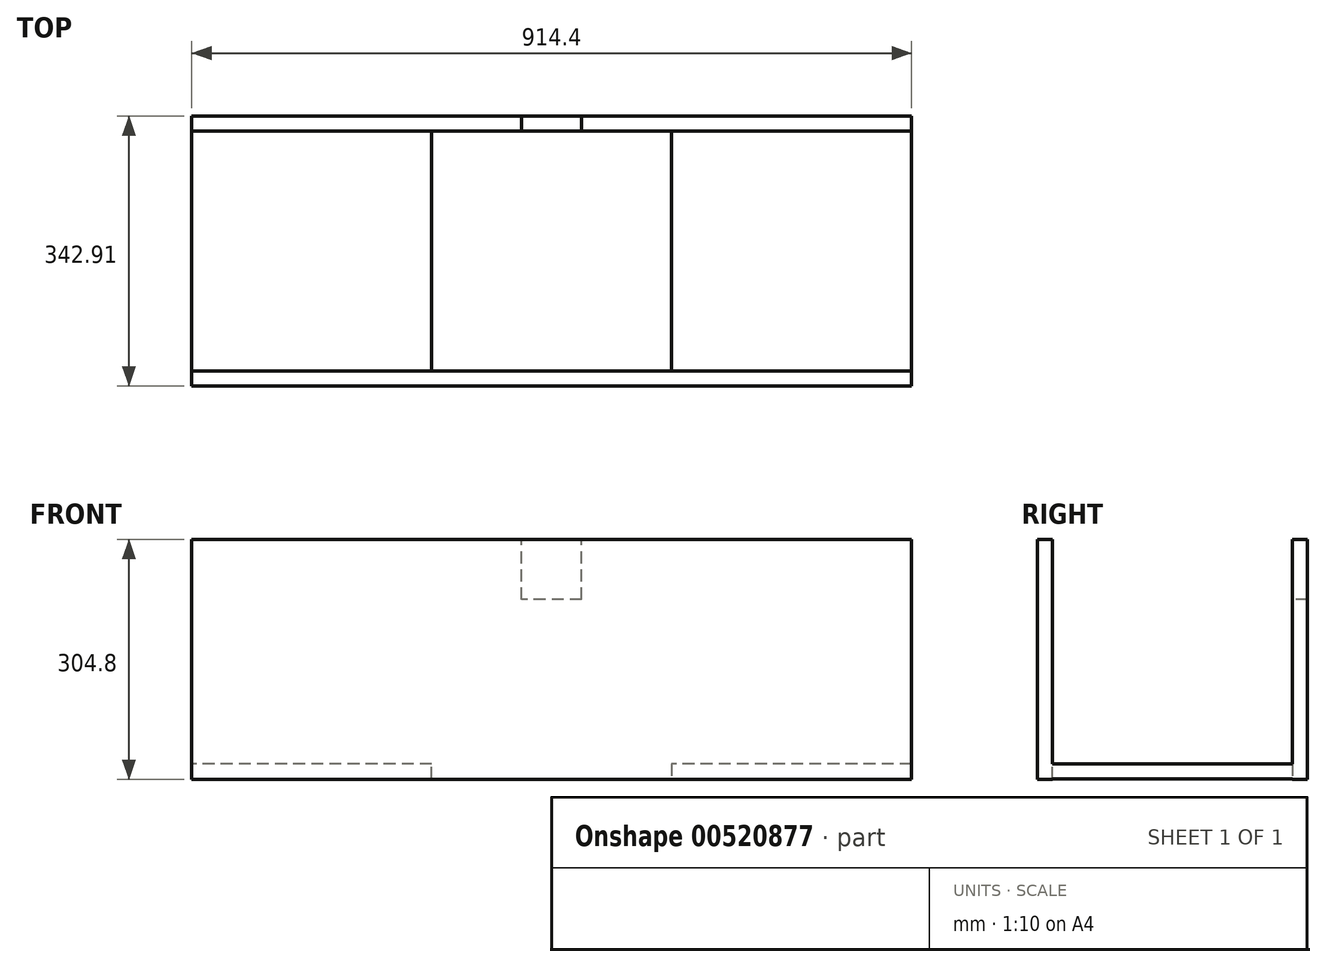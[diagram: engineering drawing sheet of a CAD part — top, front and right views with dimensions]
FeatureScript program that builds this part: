
annotation { "Feature Type Name" : "Feature", "Feature Type Description" : "" }
export const myFeature = defineFeature(function(context is Context, id is Id, definition is map)
    precondition{}
    {
        {
            var Q0;
            Q0=qCreatedBy(makeId("Top.planeOp"),FACE);
            var sketch = newSketch(context, id + "F0", { "sketchPlane" : qUnion([Q0])});
            skLineSegment(sketch, "E0.bottom", {"start": v(457.2, 9.53) * mm, "end": v(-457.2, 9.52) * mm});
            skLineSegment(sketch, "E0.top", {"start": v(457.2, -9.52) * mm, "end": v(-457.2, -9.53) * mm});
            skLineSegment(sketch, "E0.left", {"start": v(457.2, 9.53) * mm, "end": v(457.2, -9.52) * mm});
            skLineSegment(sketch, "E0.right", {"start": v(-457.2, 9.52) * mm, "end": v(-457.2, -9.53) * mm});
            skPoint(sketch, "E0.middle", {"position": v(0, 0) * mm});
            skSolve(sketch);
        }
        {
            var Q0;
            Q0 = qSketchRegion(id + "F0", true);
            extrude(context, id + "F1", {"entities" : qUnion([Q0]), "depth" : 304.8 * mm, "offsetDistance" : 25.4 * mm});
        }
        {
            var Q0;
            Q0=makeQuery(id+"F1.opExtrude","SWEPT_FACE",FACE,{"disambiguationData":[OSD([sQuery(id+"F0.wireOp",EDGE,"E0.top")])]});
            var sketch = newSketch(context, id + "F2", { "sketchPlane" : qUnion([Q0])});
            skLineSegment(sketch, "E1.bottom", {"start": v(38.1, 228.6) * mm, "end": v(-38.1, 228.6) * mm});
            skLineSegment(sketch, "E1.top", {"start": v(38.1, 381) * mm, "end": v(-38.1, 381) * mm});
            skLineSegment(sketch, "E1.left", {"start": v(38.1, 228.6) * mm, "end": v(38.1, 381) * mm});
            skLineSegment(sketch, "E1.right", {"start": v(-38.1, 228.6) * mm, "end": v(-38.1, 381) * mm});
            skPoint(sketch, "E1.middle", {"position": v(0, 304.8) * mm});
            skSolve(sketch);
        }
        {
            var Q0;
            {var subQ0=sQuery(id+"F2.wireOp",EDGE,"E1.bottom");Q0=makeQuery(id+"F2.imprint","IMPRINT",FACE,{"disambiguationData":[TD([[makeQuery(id+"F2.imprint","IMPRINT",EDGE,{"derivedFrom":subQ0}),-1.0]])]});}
            extrude(context, id + "F3", {"entities" : qUnion([Q0]), "operationType" : NewBodyOperationType.REMOVE, "oppositeDirection" : true, "depth" : 19.05 * mm, "offsetDistance" : 25.4 * mm});
        }
        {
            var Q0;
            Q0=makeQuery(id+"F1.opExtrude","SWEPT_FACE",FACE,{"disambiguationData":[OSD([sQuery(id+"F0.wireOp",EDGE,"E0.top")])]});
            var sketch = newSketch(context, id + "F4", { "sketchPlane" : qUnion([Q0])});
            skLineSegment(sketch, "E2", {"start": v(-457.2, 0) * mm, "end": v(-457.2, 0.76) * mm});
            skLineSegment(sketch, "E3", {"start": v(-457.2, 0.76) * mm, "end": v(-152.4, 0.76) * mm});
            skLineSegment(sketch, "E4", {"start": v(-152.4, 0.76) * mm, "end": v(-152.4, 19.81) * mm});
            skLineSegment(sketch, "E5", {"start": v(-152.4, 19.81) * mm, "end": v(-457.2, 19.81) * mm});
            skLineSegment(sketch, "E6", {"start": v(-457.2, 19.81) * mm, "end": v(-457.2, 0.76) * mm});
            skSolve(sketch);
        }
        {
            var Q0;
            Q0=makeQuery(id+"F4.imprint","IMPRINT",FACE,{"disambiguationData":[TD([[makeQuery(id+"F4.imprint","IMPRINT",EDGE,{"derivedFrom":sQuery(id+"F4.wireOp",EDGE,"E3")}),1.0]])]});
            extrude(context, id + "F5", {"entities" : qUnion([Q0]), "operationType" : NewBodyOperationType.ADD, "depth" : 304.8 * mm, "offsetDistance" : 25.4 * mm});
        }
        {
            var Q0;
            Q0=makeQuery(id+"F1.opExtrude","SWEPT_FACE",FACE,{"disambiguationData":[OSD([sQuery(id+"F0.wireOp",EDGE,"E0.top")])]});
            var sketch = newSketch(context, id + "F6", { "sketchPlane" : qUnion([Q0])});
            skLineSegment(sketch, "E7", {"start": v(457.2, 0) * mm, "end": v(457.2, 0.76) * mm});
            skLineSegment(sketch, "E8", {"start": v(457.2, 0.76) * mm, "end": v(457.2, 19.81) * mm});
            skLineSegment(sketch, "E9", {"start": v(457.2, 19.81) * mm, "end": v(152.4, 19.81) * mm});
            skLineSegment(sketch, "E10", {"start": v(152.4, 19.81) * mm, "end": v(152.4, 0.76) * mm});
            skLineSegment(sketch, "E11", {"start": v(152.4, 0.76) * mm, "end": v(457.2, 0.76) * mm});
            skSolve(sketch);
        }
        {
            var Q0;
            Q0=makeQuery(id+"F6.imprint","IMPRINT",FACE,{"disambiguationData":[TD([[makeQuery(id+"F6.imprint","IMPRINT",EDGE,{"derivedFrom":sQuery(id+"F6.wireOp",EDGE,"E8")}),-1.0]])]});
            extrude(context, id + "F7", {"entities" : qUnion([Q0]), "operationType" : NewBodyOperationType.ADD, "depth" : 304.8 * mm, "offsetDistance" : 25.4 * mm});
        }
        {
            var Q0;
            Q0=makeQuery(id+"F5.opExtrude","CAP_FACE",FACE,{"disambiguationData":[OSD([sQuery(id+"F4.wireOp",EDGE,"E3"),sQuery(id+"F4.wireOp",EDGE,"E4"),sQuery(id+"F4.wireOp",EDGE,"E5"),sQuery(id+"F4.wireOp",EDGE,"E6")])],"isStart":false});
            var sketch = newSketch(context, id + "F8", { "sketchPlane" : qUnion([Q0])});
            skLineSegment(sketch, "E12", {"start": v(-457.2, 0.76) * mm, "end": v(-457.2, 0) * mm});
            skLineSegment(sketch, "E13", {"start": v(-457.2, 0) * mm, "end": v(-457.2, 304.8) * mm});
            skPoint(sketch, "E13.endSnap0", {"position": v(-457.2, 10.29) * mm});
            skLineSegment(sketch, "E14", {"start": v(-457.2, 304.8) * mm, "end": v(457.2, 304.8) * mm});
            skLineSegment(sketch, "E15", {"start": v(457.2, 304.8) * mm, "end": v(457.2, 0) * mm});
            skLineSegment(sketch, "E16", {"start": v(457.2, 0) * mm, "end": v(-457.2, 0) * mm});
            skSolve(sketch);
        }
        {
            var Q0;
            {var subQ0=sQuery(id+"F8.wireOp",EDGE,"E14");Q0=makeQuery(id+"F8.imprint","IMPRINT",FACE,{"disambiguationData":[TD([[makeQuery(id+"F8.imprint","IMPRINT",EDGE,{"derivedFrom":subQ0}),-1.0]])]});}
            var Q1;
            {var subQ1=makeQuery(id+"F5.opExtrude","CAP_EDGE",EDGE,{"disambiguationData":[OSD([sQuery(id+"F4.wireOp",EDGE,"E3")])],"isStart":false});Q1=makeQuery(id+"F8.imprint","IMPRINT",FACE,{"disambiguationData":[TD([[makeQuery(id+"F8.imprint","IMPRINT",EDGE,{"derivedFrom":subQ1}),1.0]])]});}
            extrude(context, id + "F9", {"entities" : qUnion([Q0, Q1]), "operationType" : NewBodyOperationType.ADD, "depth" : 19.05 * mm, "offsetDistance" : 25.4 * mm});
        }
    });
